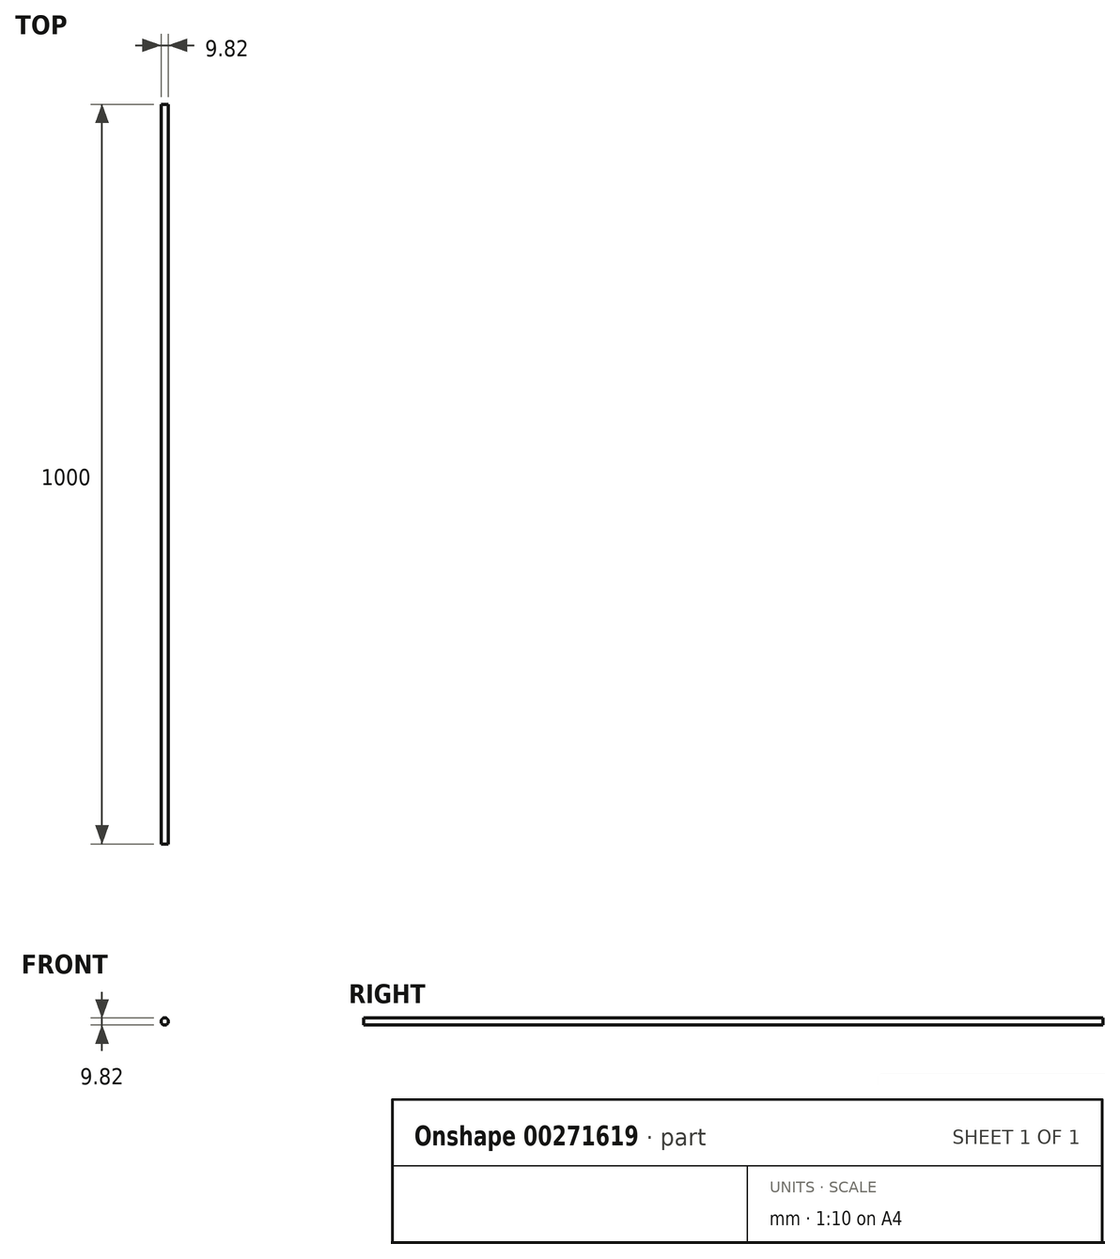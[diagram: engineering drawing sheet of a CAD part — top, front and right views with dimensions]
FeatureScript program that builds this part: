
annotation { "Feature Type Name" : "Feature", "Feature Type Description" : "" }
export const myFeature = defineFeature(function(context is Context, id is Id, definition is map)
    precondition{}
    {
        {
            var Q0;
            Q0=qCreatedBy(makeId("Front.planeOp"),FACE);
            var sketch = newSketch(context, id + "F0", { "sketchPlane" : qUnion([Q0])});
            skCircle(sketch, "E0", {"center": v(-0.09, -0.15) * mm, "radius": 4.91 * mm});
            skSolve(sketch);
        }
        {
            var Q0;
            Q0 = qSketchRegion(id + "F0", true);
            extrude(context, id + "F1", {"entities" : qUnion([Q0]), "depth" : 1000 * mm});
        }
    });
